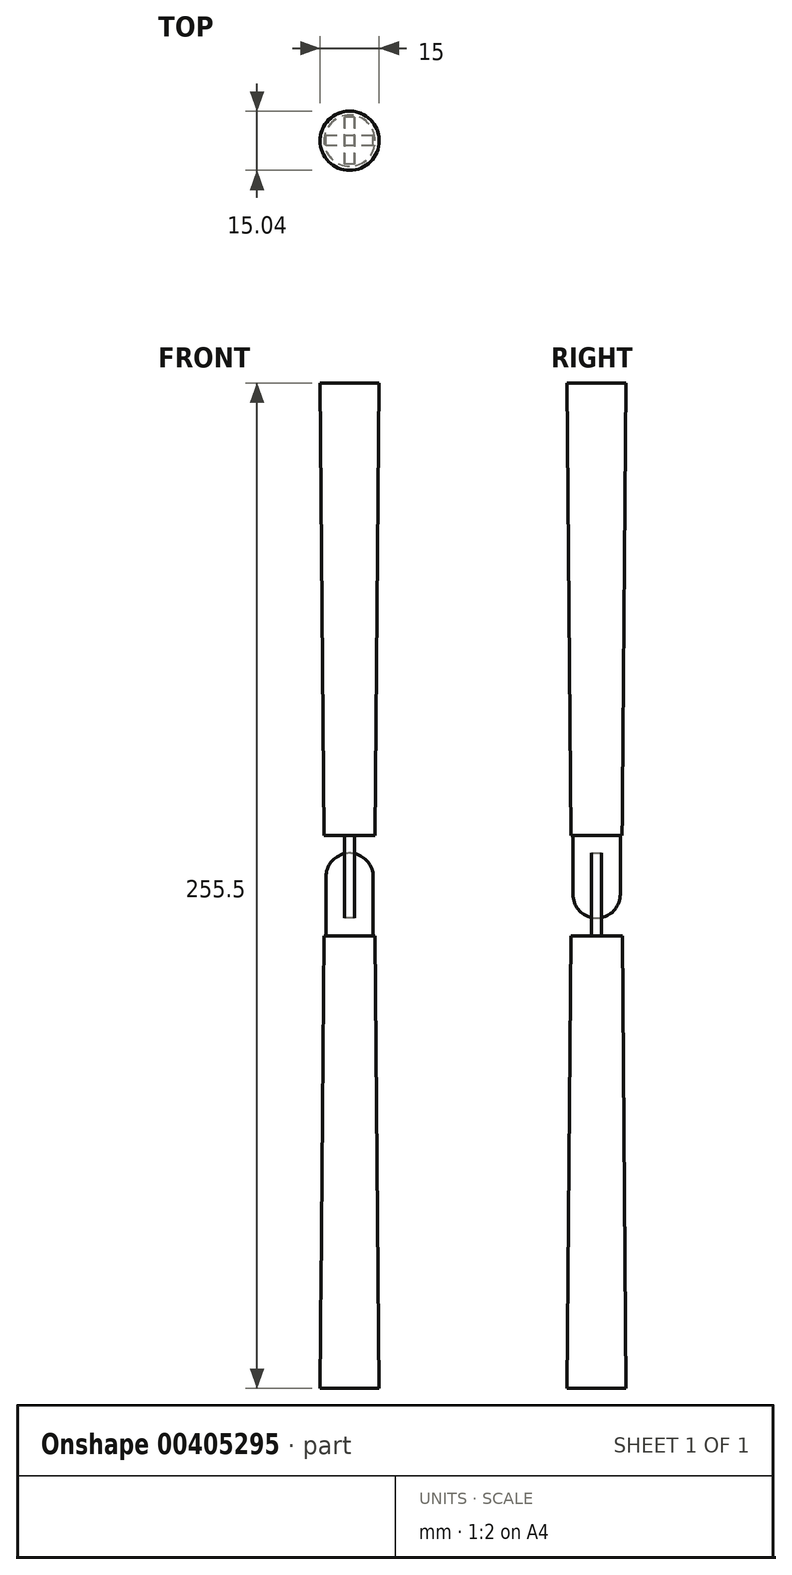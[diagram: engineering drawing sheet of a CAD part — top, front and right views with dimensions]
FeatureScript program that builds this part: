
annotation { "Feature Type Name" : "Feature", "Feature Type Description" : "" }
export const myFeature = defineFeature(function(context is Context, id is Id, definition is map)
    precondition{}
    {
        {
            var Q0;
            Q0=qCreatedBy(makeId("Front.planeOp"),FACE);
            var sketch = newSketch(context, id + "F0", { "sketchPlane" : qUnion([Q0])});
            skLineSegment(sketch, "E0.bottom", {"start": v(0, 0) * mm, "end": v(-6, 0) * mm});
            skLineSegment(sketch, "E0.top", {"start": v(0, 15) * mm, "end": v(-6, 15) * mm});
            skLineSegment(sketch, "E0.left", {"start": v(0, 0) * mm, "end": v(0, 15) * mm});
            skLineSegment(sketch, "E0.right", {"start": v(-6, 0) * mm, "end": v(-6, 15) * mm});
            skLineSegment(sketch, "E1.bottom", {"start": v(0, 0) * mm, "end": v(6, 0) * mm});
            skLineSegment(sketch, "E1.top", {"start": v(0, 15) * mm, "end": v(6, 15) * mm});
            skLineSegment(sketch, "E1.right", {"start": v(6, 0) * mm, "end": v(6, 15) * mm});
            skArc(sketch, "E2", {"start": v(-6, 15) * mm, "mid": v(0, 21) * mm, "end": v(6, 15) * mm});
            skLineSegment(sketch, "E3", {"start": v(0, 0) * mm, "end": v(-6.5, 0) * mm});
            skLineSegment(sketch, "E4", {"start": v(-6.5, 0) * mm, "end": v(-7.5, -115) * mm});
            skLineSegment(sketch, "E5", {"start": v(-7.5, -115) * mm, "end": v(0, -115) * mm});
            skLineSegment(sketch, "E6", {"start": v(0, -115) * mm, "end": v(0, 0) * mm});
            skSolve(sketch);
        }
        {
            var Q0;
            {var subQ0=sQuery(id+"F0.wireOp",EDGE,"E4");Q0=makeQuery(id+"F0.imprint","IMPRINT",FACE,{"disambiguationData":[TD([[makeQuery(id+"F0.imprint","IMPRINT",EDGE,{"derivedFrom":subQ0}),1.0]])]});}
            var Q1;
            Q1=qSketchRegion(id+"F3",true);
            var Q2;
            Q2=sQuery(id+"F0.wireOp",EDGE,"E6");
            revolve(context, id + "F1", {"entities" : qUnion([Q0, Q1]), "axis" : qUnion([Q2]), "revolveType" : RevolveType.FULL});
        }
        {
            var Q0;
            Q0=makeQuery(id+"F0.imprint","IMPRINT",FACE,{"disambiguationData":[TD([[makeQuery(id+"F0.imprint","IMPRINT",EDGE,{"derivedFrom":sQuery(id+"F0.wireOp",EDGE,"E0.top")}),1.0]])]});
            var Q1;
            Q1=makeQuery(id+"F0.imprint","IMPRINT",FACE,{"disambiguationData":[TD([[makeQuery(id+"F0.imprint","IMPRINT",EDGE,{"derivedFrom":sQuery(id+"F0.wireOp",EDGE,"E1.bottom")}),1.0]])]});
            var Q2;
            Q2=makeQuery(id+"F0.imprint","IMPRINT",FACE,{"disambiguationData":[TD([[makeQuery(id+"F0.imprint","IMPRINT",EDGE,{"derivedFrom":sQuery(id+"F0.wireOp",EDGE,"E0.top")}),-1.0]])]});
            extrude(context, id + "F2", {"entities" : qUnion([Q0, Q1, Q2]), "operationType" : NewBodyOperationType.ADD, "endBound" : BoundingType.SYMMETRIC, "depth" : 2.5 * mm});
        }
        {
            var Q0;
            Q0=qCreatedBy(makeId("Right.planeOp"),FACE);
            var sketch = newSketch(context, id + "F3", { "sketchPlane" : qUnion([Q0])});
            skLineSegment(sketch, "E7.bottom", {"start": v(0, 25.5) * mm, "end": v(6, 25.5) * mm});
            skLineSegment(sketch, "E7.top", {"start": v(0, 10.5) * mm, "end": v(6, 10.5) * mm});
            skLineSegment(sketch, "E7.left", {"start": v(0, 25.5) * mm, "end": v(0, 10.5) * mm});
            skLineSegment(sketch, "E7.right", {"start": v(6, 25.5) * mm, "end": v(6, 10.5) * mm});
            skLineSegment(sketch, "E8.bottom", {"start": v(0, 25.5) * mm, "end": v(-6, 25.5) * mm});
            skLineSegment(sketch, "E8.top", {"start": v(0, 10.5) * mm, "end": v(-6, 10.5) * mm});
            skLineSegment(sketch, "E8.right", {"start": v(-6, 25.5) * mm, "end": v(-6, 10.5) * mm});
            skArc(sketch, "E9", {"start": v(6, 10.5) * mm, "mid": v(0, 4.5) * mm, "end": v(-6, 10.5) * mm});
            skPoint(sketch, "E10.endSnap0", {"position": v(0, 4.5) * mm});
            skLineSegment(sketch, "E11", {"start": v(0, 6) * mm, "end": v(0, 4.5) * mm});
            skLineSegment(sketch, "E12.MirrorCS", {"start": v(-7.54, 140.5) * mm, "end": v(-0.04, 140.5) * mm});
            skLineSegment(sketch, "E13.MirrorCS", {"start": v(-6.54, 25.5) * mm, "end": v(-7.54, 140.5) * mm});
            skLineSegment(sketch, "E14.MirrorCS", {"start": v(-0.04, 25.5) * mm, "end": v(-6.54, 25.5) * mm});
            skLineSegment(sketch, "E15.MirrorCS", {"start": v(-0.04, 25.5) * mm, "end": v(-0.04, 140.5) * mm});
            skSolve(sketch);
        }
        {
            var Q0;
            Q0=makeQuery(id+"F3.imprint","IMPRINT",FACE,{"disambiguationData":[TD([[makeQuery(id+"F3.imprint","IMPRINT",EDGE,{"derivedFrom":sQuery(id+"F3.wireOp",EDGE,"E12.MirrorCS")}),-1.0]])]});
            var Q1;
            Q1=sQuery(id+"F3.wireOp",EDGE,"E15.MirrorCS");
            revolve(context, id + "F4", {"entities" : qUnion([Q0]), "axis" : qUnion([Q1]), "revolveType" : RevolveType.FULL});
        }
        {
            var Q0;
            {var subQ1=sQuery(id+"F3.wireOp",EDGE,"E8.bottom");Q0=makeQuery(id+"F3.imprint","IMPRINT",FACE,{"disambiguationData":[TD([[makeQuery(id+"F3.imprint","IMPRINT",EDGE,{"derivedFrom":subQ1}),1.0]])]});}
            var Q1;
            Q1=makeQuery(id+"F3.imprint","IMPRINT",FACE,{"disambiguationData":[TD([[makeQuery(id+"F3.imprint","IMPRINT",EDGE,{"derivedFrom":sQuery(id+"F3.wireOp",EDGE,"E7.bottom")}),-1.0]])]});
            var Q2;
            {var subQ0=sQuery(id+"F3.wireOp",EDGE,"E7.top");Q2=makeQuery(id+"F3.imprint","IMPRINT",FACE,{"disambiguationData":[TD([[makeQuery(id+"F3.imprint","IMPRINT",EDGE,{"derivedFrom":subQ0}),-1.0]])]});}
            extrude(context, id + "F5", {"entities" : qUnion([Q0, Q1, Q2]), "endBound" : BoundingType.SYMMETRIC, "depth" : 2.5 * mm});
        }
    });
